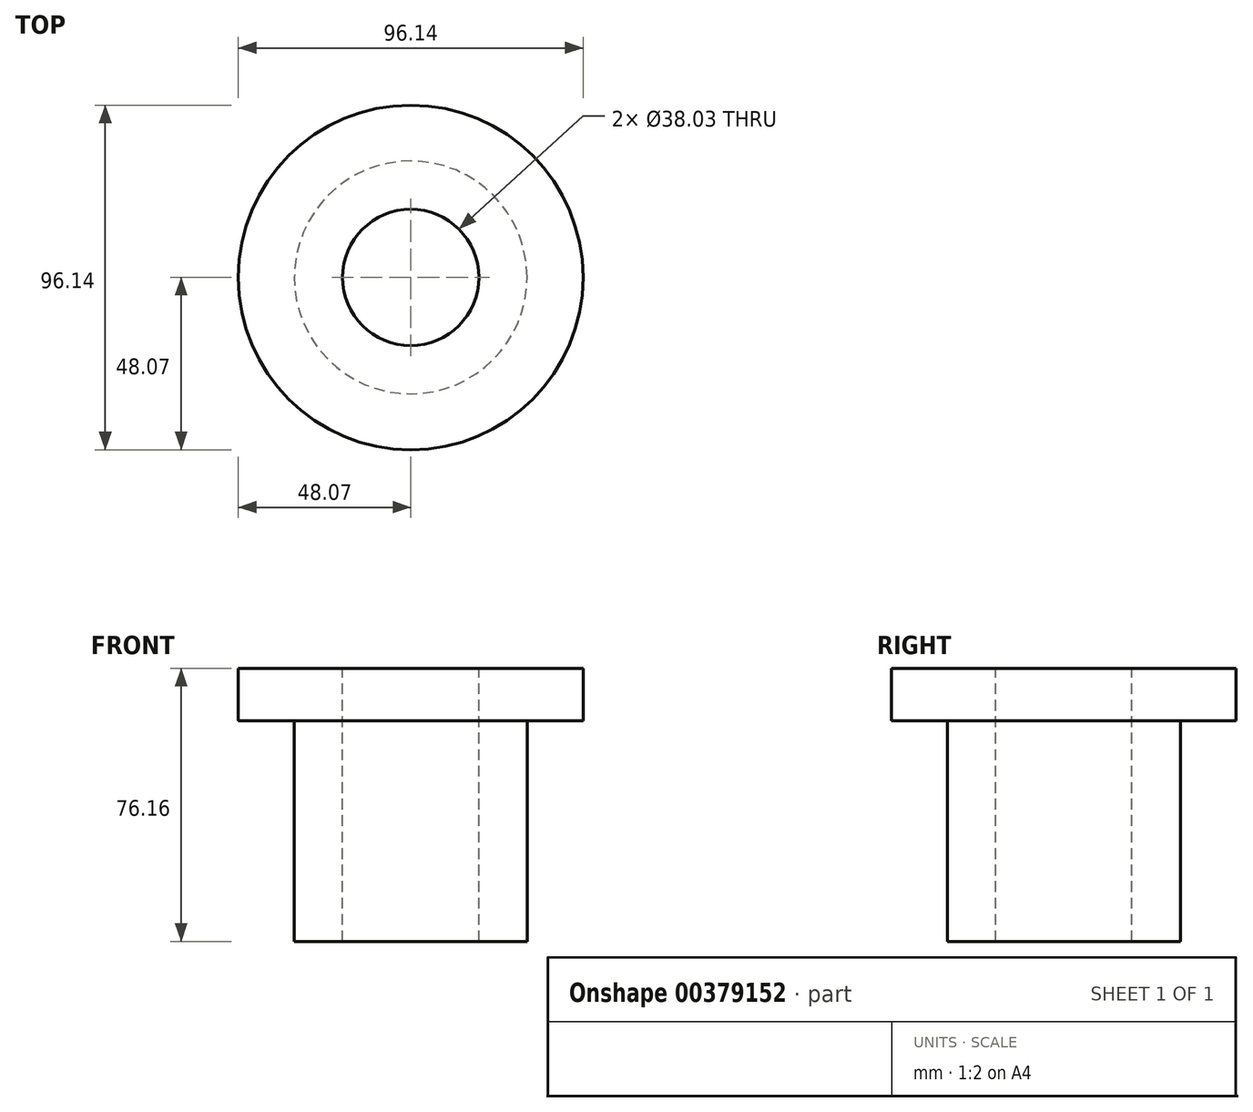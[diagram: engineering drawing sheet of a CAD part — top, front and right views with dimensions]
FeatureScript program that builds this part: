
annotation { "Feature Type Name" : "Feature", "Feature Type Description" : "" }
export const myFeature = defineFeature(function(context is Context, id is Id, definition is map)
    precondition{}
    {
        {
            var Q0;
            Q0=qCreatedBy(makeId("Front.planeOp"),FACE);
            var sketch = newSketch(context, id + "F0", { "sketchPlane" : qUnion([Q0])});
            skLineSegment(sketch, "E0", {"start": v(19.01, -76.16) * mm, "end": v(19.01, 0) * mm});
            skLineSegment(sketch, "E1", {"start": v(19.01, 0) * mm, "end": v(48.07, 0) * mm});
            skLineSegment(sketch, "E2", {"start": v(48.07, 0) * mm, "end": v(48.07, -14.63) * mm});
            skLineSegment(sketch, "E3", {"start": v(48.07, -14.63) * mm, "end": v(32.47, -14.63) * mm});
            skLineSegment(sketch, "E4", {"start": v(32.47, -14.63) * mm, "end": v(32.47, -76.16) * mm});
            skLineSegment(sketch, "E5", {"start": v(32.47, -76.16) * mm, "end": v(19.01, -76.16) * mm});
            skLineSegment(sketch, "E6", {"start": v(0, 75.95) * mm, "end": v(0, -76.38) * mm});
            skSolve(sketch);
        }
        {
            var Q0;
            Q0=makeQuery(id+"F0.imprint","IMPRINT",FACE,{"disambiguationData":[TD([[makeQuery(id+"F0.imprint","IMPRINT",EDGE,{"derivedFrom":sQuery(id+"F0.wireOp",EDGE,"E0")}),-1.0]])]});
            var Q1;
            Q1=sQuery(id+"F0.wireOp",EDGE,"E6");
            revolve(context, id + "F1", {"entities" : qUnion([Q0]), "axis" : qUnion([Q1]), "revolveType" : RevolveType.FULL});
        }
        {
            var Q0;
            Q0=qCreatedBy(makeId("Right.planeOp"),FACE);
            var sketch = newSketch(context, id + "F2", { "sketchPlane" : qUnion([Q0])});
            skLineSegment(sketch, "E7", {"start": v(0, -76.1) * mm, "end": v(0, 76.85) * mm});
            skSolve(sketch);
        }
        {
            var Q0;
            Q0=makeQuery(id+"F1.opRevolve","SWEPT_BODY",BODY,{"disambiguationData":[OSD([sQuery(id+"F0.wireOp",EDGE,"E0"),sQuery(id+"F0.wireOp",EDGE,"E1"),sQuery(id+"F0.wireOp",EDGE,"E2"),sQuery(id+"F0.wireOp",EDGE,"E3"),sQuery(id+"F0.wireOp",EDGE,"E4"),sQuery(id+"F0.wireOp",EDGE,"E5")])]});
            var Q1;
            Q1=sQuery(id+"F2.wireOp",EDGE,"E7");
            transform(context, id + "F3", {"entities" : qUnion([Q0]), "transformType" : TransformType.ROTATION, "transformAxis" : qUnion([Q1]), "angle" : 135 * degree, "makeCopy" : true});
        }
    });
